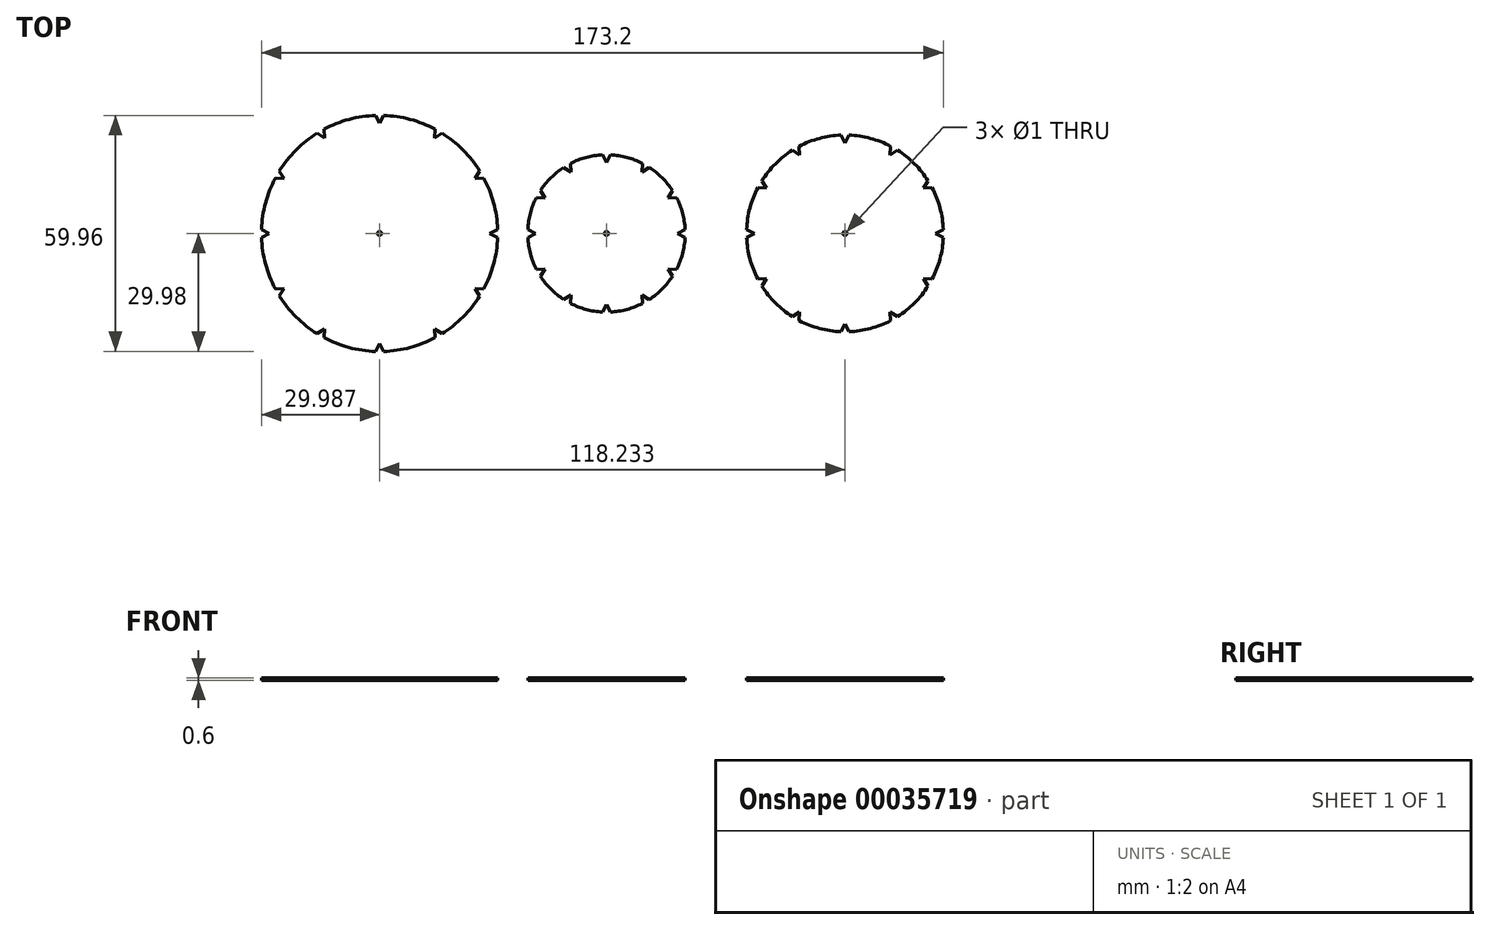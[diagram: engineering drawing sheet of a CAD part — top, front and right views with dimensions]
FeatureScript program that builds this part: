
annotation { "Feature Type Name" : "Feature", "Feature Type Description" : "" }
export const myFeature = defineFeature(function(context is Context, id is Id, definition is map)
    precondition{}
    {
        {
            var Q0;
            Q0=qCreatedBy(makeId("Top.planeOp"),FACE);
            var sketch = newSketch(context, id + "F0", { "sketchPlane" : qUnion([Q0])});
            skArc(sketch, "E0", {"start": v(9.12, 17.8) * mm, "mid": v(5.18, 19.32) * mm, "end": v(1, 19.97) * mm});
            skLineSegment(sketch, "E1", {"start": v(-1, 19.97) * mm, "end": v(0, 18) * mm});
            skLineSegment(sketch, "E2", {"start": v(0, 18) * mm, "end": v(1, 19.97) * mm});
            skLineSegment(sketch, "E3.1.0", {"start": v(9.12, 17.8) * mm, "end": v(9, 15.59) * mm});
            skLineSegment(sketch, "E3.1.1", {"start": v(9, 15.59) * mm, "end": v(10.85, 16.8) * mm});
            skLineSegment(sketch, "E3.2.0", {"start": v(16.8, 10.85) * mm, "end": v(15.59, 9) * mm});
            skLineSegment(sketch, "E3.2.1", {"start": v(15.59, 9) * mm, "end": v(17.8, 9.12) * mm});
            skLineSegment(sketch, "E3.3.0", {"start": v(19.97, 1) * mm, "end": v(18, 0) * mm});
            skLineSegment(sketch, "E3.3.1", {"start": v(18, 0) * mm, "end": v(19.97, -1) * mm});
            skLineSegment(sketch, "E3.4.0", {"start": v(17.8, -9.12) * mm, "end": v(15.59, -9) * mm});
            skLineSegment(sketch, "E3.4.1", {"start": v(15.59, -9) * mm, "end": v(16.8, -10.85) * mm});
            skLineSegment(sketch, "E3.5.0", {"start": v(10.85, -16.8) * mm, "end": v(9, -15.59) * mm});
            skLineSegment(sketch, "E3.5.1", {"start": v(9, -15.59) * mm, "end": v(9.12, -17.8) * mm});
            skLineSegment(sketch, "E3.6.0", {"start": v(1, -19.97) * mm, "end": v(0, -18) * mm});
            skLineSegment(sketch, "E3.6.1", {"start": v(0, -18) * mm, "end": v(-1, -19.97) * mm});
            skLineSegment(sketch, "E3.7.0", {"start": v(-9.12, -17.8) * mm, "end": v(-9, -15.59) * mm});
            skLineSegment(sketch, "E3.7.1", {"start": v(-9, -15.59) * mm, "end": v(-10.85, -16.8) * mm});
            skLineSegment(sketch, "E3.8.0", {"start": v(-16.8, -10.85) * mm, "end": v(-15.59, -9) * mm});
            skLineSegment(sketch, "E3.8.1", {"start": v(-15.59, -9) * mm, "end": v(-17.8, -9.12) * mm});
            skLineSegment(sketch, "E3.9.0", {"start": v(-19.97, -1) * mm, "end": v(-18, 0) * mm});
            skLineSegment(sketch, "E3.9.1", {"start": v(-18, 0) * mm, "end": v(-19.97, 1) * mm});
            skLineSegment(sketch, "E3.10.0", {"start": v(-17.8, 9.12) * mm, "end": v(-15.59, 9) * mm});
            skLineSegment(sketch, "E3.10.1", {"start": v(-15.59, 9) * mm, "end": v(-16.8, 10.85) * mm});
            skLineSegment(sketch, "E3.11.0", {"start": v(-10.85, 16.8) * mm, "end": v(-9, 15.59) * mm});
            skLineSegment(sketch, "E3.11.1", {"start": v(-9, 15.59) * mm, "end": v(-9.12, 17.8) * mm});
            skLineSegment(sketch, "E3.anchor1", {"start": v(0, 0) * mm, "end": v(0, 18) * mm, "construction": true});
            skLineSegment(sketch, "E3.anchor2", {"start": v(0, 0) * mm, "end": v(-9, 15.59) * mm, "construction": true});
            skArc(sketch, "E4.trimOffspring", {"start": v(16.8, 10.85) * mm, "mid": v(14.14, 14.14) * mm, "end": v(10.85, 16.8) * mm});
            skArc(sketch, "E5.trimOffspring", {"start": v(19.97, 1) * mm, "mid": v(19.32, 5.18) * mm, "end": v(17.8, 9.12) * mm});
            skArc(sketch, "E6.trimOffspring", {"start": v(17.8, -9.12) * mm, "mid": v(19.32, -5.18) * mm, "end": v(19.97, -1) * mm});
            skArc(sketch, "E7.trimOffspring", {"start": v(-10.85, 16.8) * mm, "mid": v(-14.14, 14.14) * mm, "end": v(-16.8, 10.85) * mm});
            skArc(sketch, "E8.trimOffspring", {"start": v(-17.8, 9.12) * mm, "mid": v(-19.32, 5.18) * mm, "end": v(-19.97, 1) * mm});
            skArc(sketch, "E9.trimOffspring", {"start": v(-19.97, -1) * mm, "mid": v(-19.32, -5.18) * mm, "end": v(-17.8, -9.12) * mm});
            skArc(sketch, "E10.trimOffspring", {"start": v(-16.8, -10.85) * mm, "mid": v(-14.14, -14.14) * mm, "end": v(-10.85, -16.8) * mm});
            skArc(sketch, "E11.trimOffspring", {"start": v(-9.12, -17.8) * mm, "mid": v(-5.18, -19.32) * mm, "end": v(-1, -19.97) * mm});
            skArc(sketch, "E12.trimOffspring", {"start": v(1, -19.97) * mm, "mid": v(5.18, -19.32) * mm, "end": v(9.12, -17.8) * mm});
            skArc(sketch, "E13.trimOffspring", {"start": v(10.85, -16.8) * mm, "mid": v(14.14, -14.14) * mm, "end": v(16.8, -10.85) * mm});
            skArc(sketch, "E14.trimOffspring", {"start": v(-1, 19.97) * mm, "mid": v(-5.18, 19.32) * mm, "end": v(-9.12, 17.8) * mm});
            skCircle(sketch, "E15", {"center": v(0, 0) * mm, "radius": 0.5 * mm});
            skArc(sketch, "E16", {"start": v(72.2, 22.13) * mm, "mid": v(67.05, 24.15) * mm, "end": v(61.58, 24.98) * mm});
            skCircle(sketch, "E17", {"center": v(60.58, 0) * mm, "radius": 0.5 * mm});
            skLineSegment(sketch, "E18", {"start": v(60.58, 0) * mm, "end": v(60.58, 29.32) * mm, "construction": true});
            skLineSegment(sketch, "E19", {"start": v(59.58, 24.98) * mm, "end": v(60.58, 23) * mm});
            skLineSegment(sketch, "E20", {"start": v(60.58, 23) * mm, "end": v(61.58, 24.98) * mm});
            skLineSegment(sketch, "E21.1.0", {"start": v(47.22, 21.13) * mm, "end": v(49.08, 19.92) * mm});
            skLineSegment(sketch, "E21.1.1", {"start": v(49.08, 19.92) * mm, "end": v(48.96, 22.13) * mm});
            skLineSegment(sketch, "E21.2.0", {"start": v(38.45, 11.62) * mm, "end": v(40.66, 11.5) * mm});
            skLineSegment(sketch, "E21.2.1", {"start": v(40.66, 11.5) * mm, "end": v(39.45, 13.36) * mm});
            skLineSegment(sketch, "E21.3.0", {"start": v(35.6, -1) * mm, "end": v(37.58, 0) * mm});
            skLineSegment(sketch, "E21.3.1", {"start": v(37.58, 0) * mm, "end": v(35.6, 1) * mm});
            skLineSegment(sketch, "E21.4.0", {"start": v(39.45, -13.36) * mm, "end": v(40.66, -11.5) * mm});
            skLineSegment(sketch, "E21.4.1", {"start": v(40.66, -11.5) * mm, "end": v(38.45, -11.62) * mm});
            skLineSegment(sketch, "E21.5.0", {"start": v(48.96, -22.13) * mm, "end": v(49.08, -19.92) * mm});
            skLineSegment(sketch, "E21.5.1", {"start": v(49.08, -19.92) * mm, "end": v(47.22, -21.13) * mm});
            skLineSegment(sketch, "E21.6.0", {"start": v(61.58, -24.98) * mm, "end": v(60.58, -23) * mm});
            skLineSegment(sketch, "E21.6.1", {"start": v(60.58, -23) * mm, "end": v(59.58, -24.98) * mm});
            skLineSegment(sketch, "E21.7.0", {"start": v(73.94, -21.13) * mm, "end": v(72.08, -19.92) * mm});
            skLineSegment(sketch, "E21.7.1", {"start": v(72.08, -19.92) * mm, "end": v(72.2, -22.13) * mm});
            skLineSegment(sketch, "E21.8.0", {"start": v(82.71, -11.62) * mm, "end": v(80.5, -11.5) * mm});
            skLineSegment(sketch, "E21.8.1", {"start": v(80.5, -11.5) * mm, "end": v(81.71, -13.36) * mm});
            skLineSegment(sketch, "E21.9.0", {"start": v(85.56, 1) * mm, "end": v(83.58, 0) * mm});
            skLineSegment(sketch, "E21.9.1", {"start": v(83.58, 0) * mm, "end": v(85.56, -1) * mm});
            skLineSegment(sketch, "E21.10.0", {"start": v(81.71, 13.36) * mm, "end": v(80.5, 11.5) * mm});
            skLineSegment(sketch, "E21.10.1", {"start": v(80.5, 11.5) * mm, "end": v(82.71, 11.62) * mm});
            skLineSegment(sketch, "E21.11.0", {"start": v(72.2, 22.13) * mm, "end": v(72.08, 19.92) * mm});
            skLineSegment(sketch, "E21.11.1", {"start": v(72.08, 19.92) * mm, "end": v(73.94, 21.13) * mm});
            skArc(sketch, "E22.trimOffspring", {"start": v(81.71, 13.36) * mm, "mid": v(78.26, 17.68) * mm, "end": v(73.94, 21.13) * mm});
            skArc(sketch, "E23.trimOffspring", {"start": v(85.56, 1) * mm, "mid": v(84.73, 6.47) * mm, "end": v(82.71, 11.62) * mm});
            skArc(sketch, "E24.trimOffspring", {"start": v(82.71, -11.62) * mm, "mid": v(84.73, -6.47) * mm, "end": v(85.56, -1) * mm});
            skArc(sketch, "E25.trimOffspring", {"start": v(73.94, -21.13) * mm, "mid": v(78.26, -17.68) * mm, "end": v(81.71, -13.36) * mm});
            skArc(sketch, "E26.trimOffspring", {"start": v(61.58, -24.98) * mm, "mid": v(67.05, -24.15) * mm, "end": v(72.2, -22.13) * mm});
            skArc(sketch, "E27.trimOffspring", {"start": v(48.96, -22.13) * mm, "mid": v(54.1, -24.15) * mm, "end": v(59.58, -24.98) * mm});
            skArc(sketch, "E28.trimOffspring", {"start": v(39.45, -13.36) * mm, "mid": v(42.9, -17.68) * mm, "end": v(47.22, -21.13) * mm});
            skArc(sketch, "E29.trimOffspring", {"start": v(35.6, -1) * mm, "mid": v(36.43, -6.47) * mm, "end": v(38.45, -11.62) * mm});
            skArc(sketch, "E30.trimOffspring", {"start": v(38.45, 11.62) * mm, "mid": v(36.43, 6.47) * mm, "end": v(35.6, 1) * mm});
            skArc(sketch, "E31.trimOffspring", {"start": v(47.22, 21.13) * mm, "mid": v(42.9, 17.68) * mm, "end": v(39.45, 13.36) * mm});
            skArc(sketch, "E32.trimOffspring", {"start": v(59.58, 24.98) * mm, "mid": v(54.1, 24.15) * mm, "end": v(48.96, 22.13) * mm});
            skArc(sketch, "E33", {"start": v(-43.53, 26.47) * mm, "mid": v(-49.89, 28.98) * mm, "end": v(-56.65, 29.98) * mm});
            skCircle(sketch, "E34", {"center": v(-57.65, 0) * mm, "radius": 0.5 * mm});
            skLineSegment(sketch, "E35", {"start": v(-57.65, 0) * mm, "end": v(-57.65, 46.7) * mm, "construction": true});
            skLineSegment(sketch, "E36", {"start": v(-58.65, 29.98) * mm, "end": v(-57.65, 28) * mm});
            skLineSegment(sketch, "E37", {"start": v(-57.65, 28) * mm, "end": v(-56.65, 29.98) * mm});
            skLineSegment(sketch, "E38.1.0", {"start": v(-73.51, 25.47) * mm, "end": v(-71.65, 24.25) * mm});
            skLineSegment(sketch, "E38.1.1", {"start": v(-71.65, 24.25) * mm, "end": v(-71.78, 26.47) * mm});
            skLineSegment(sketch, "E38.2.0", {"start": v(-84.12, 14.13) * mm, "end": v(-81.9, 14) * mm});
            skLineSegment(sketch, "E38.2.1", {"start": v(-81.9, 14) * mm, "end": v(-83.12, 15.86) * mm});
            skLineSegment(sketch, "E38.3.0", {"start": v(-87.64, -1) * mm, "end": v(-85.65, 0) * mm});
            skLineSegment(sketch, "E38.3.1", {"start": v(-85.65, 0) * mm, "end": v(-87.64, 1) * mm});
            skLineSegment(sketch, "E38.4.0", {"start": v(-83.12, -15.86) * mm, "end": v(-81.9, -14) * mm});
            skLineSegment(sketch, "E38.4.1", {"start": v(-81.9, -14) * mm, "end": v(-84.12, -14.13) * mm});
            skLineSegment(sketch, "E38.5.0", {"start": v(-71.78, -26.47) * mm, "end": v(-71.65, -24.25) * mm});
            skLineSegment(sketch, "E38.5.1", {"start": v(-71.65, -24.25) * mm, "end": v(-73.51, -25.47) * mm});
            skLineSegment(sketch, "E38.6.0", {"start": v(-56.65, -29.98) * mm, "end": v(-57.65, -28) * mm});
            skLineSegment(sketch, "E38.6.1", {"start": v(-57.65, -28) * mm, "end": v(-58.65, -29.98) * mm});
            skLineSegment(sketch, "E38.7.0", {"start": v(-41.8, -25.47) * mm, "end": v(-43.65, -24.25) * mm});
            skLineSegment(sketch, "E38.7.1", {"start": v(-43.65, -24.25) * mm, "end": v(-43.53, -26.47) * mm});
            skLineSegment(sketch, "E38.8.0", {"start": v(-31.19, -14.13) * mm, "end": v(-33.4, -14) * mm});
            skLineSegment(sketch, "E38.8.1", {"start": v(-33.4, -14) * mm, "end": v(-32.19, -15.86) * mm});
            skLineSegment(sketch, "E38.9.0", {"start": v(-27.67, 1) * mm, "end": v(-29.65, 0) * mm});
            skLineSegment(sketch, "E38.9.1", {"start": v(-29.65, 0) * mm, "end": v(-27.67, -1) * mm});
            skLineSegment(sketch, "E38.10.0", {"start": v(-32.19, 15.86) * mm, "end": v(-33.4, 14) * mm});
            skLineSegment(sketch, "E38.10.1", {"start": v(-33.4, 14) * mm, "end": v(-31.19, 14.13) * mm});
            skLineSegment(sketch, "E38.11.0", {"start": v(-43.53, 26.47) * mm, "end": v(-43.65, 24.25) * mm});
            skLineSegment(sketch, "E38.11.1", {"start": v(-43.65, 24.25) * mm, "end": v(-41.8, 25.47) * mm});
            skArc(sketch, "E39.trimOffspring", {"start": v(-32.19, 15.86) * mm, "mid": v(-36.44, 21.21) * mm, "end": v(-41.8, 25.47) * mm});
            skArc(sketch, "E40.trimOffspring", {"start": v(-27.67, 1) * mm, "mid": v(-28.68, 7.76) * mm, "end": v(-31.19, 14.13) * mm});
            skArc(sketch, "E41.trimOffspring", {"start": v(-73.51, 25.47) * mm, "mid": v(-78.87, 21.21) * mm, "end": v(-83.12, 15.86) * mm});
            skArc(sketch, "E42.trimOffspring", {"start": v(-84.12, 14.13) * mm, "mid": v(-86.63, 7.76) * mm, "end": v(-87.64, 1) * mm});
            skArc(sketch, "E43.trimOffspring", {"start": v(-87.64, -1) * mm, "mid": v(-86.63, -7.76) * mm, "end": v(-84.12, -14.13) * mm});
            skArc(sketch, "E44.trimOffspring", {"start": v(-83.12, -15.86) * mm, "mid": v(-78.87, -21.21) * mm, "end": v(-73.51, -25.47) * mm});
            skArc(sketch, "E45.trimOffspring", {"start": v(-58.65, 29.98) * mm, "mid": v(-65.42, 28.98) * mm, "end": v(-71.78, 26.47) * mm});
            skArc(sketch, "E46.trimOffspring", {"start": v(-31.19, -14.13) * mm, "mid": v(-28.68, -7.76) * mm, "end": v(-27.67, -1) * mm});
            skArc(sketch, "E47.trimOffspring", {"start": v(-41.8, -25.47) * mm, "mid": v(-36.44, -21.21) * mm, "end": v(-32.19, -15.86) * mm});
            skArc(sketch, "E48.trimOffspring", {"start": v(-56.65, -29.98) * mm, "mid": v(-49.89, -28.98) * mm, "end": v(-43.53, -26.47) * mm});
            skArc(sketch, "E49.trimOffspring", {"start": v(-71.78, -26.47) * mm, "mid": v(-65.42, -28.98) * mm, "end": v(-58.65, -29.98) * mm});
            skSolve(sketch);
        }
        {
            var Q0;
            Q0=makeQuery(id+"F0.imprint","IMPRINT",FACE,{"disambiguationData":[TD([[makeQuery(id+"F0.imprint","IMPRINT",EDGE,{"derivedFrom":sQuery(id+"F0.wireOp",EDGE,"E16")}),1.0]])]});
            var Q1;
            Q1=makeQuery(id+"F0.imprint","IMPRINT",FACE,{"disambiguationData":[TD([[makeQuery(id+"F0.imprint","IMPRINT",EDGE,{"derivedFrom":sQuery(id+"F0.wireOp",EDGE,"E0")}),1.0]])]});
            var Q2;
            Q2=makeQuery(id+"F0.imprint","IMPRINT",FACE,{"disambiguationData":[TD([[makeQuery(id+"F0.imprint","IMPRINT",EDGE,{"derivedFrom":sQuery(id+"F0.wireOp",EDGE,"E33")}),1.0]])]});
            extrude(context, id + "F1", {"entities" : qUnion([Q0, Q1, Q2]), "depth" : 0.6 * mm});
        }
    });
